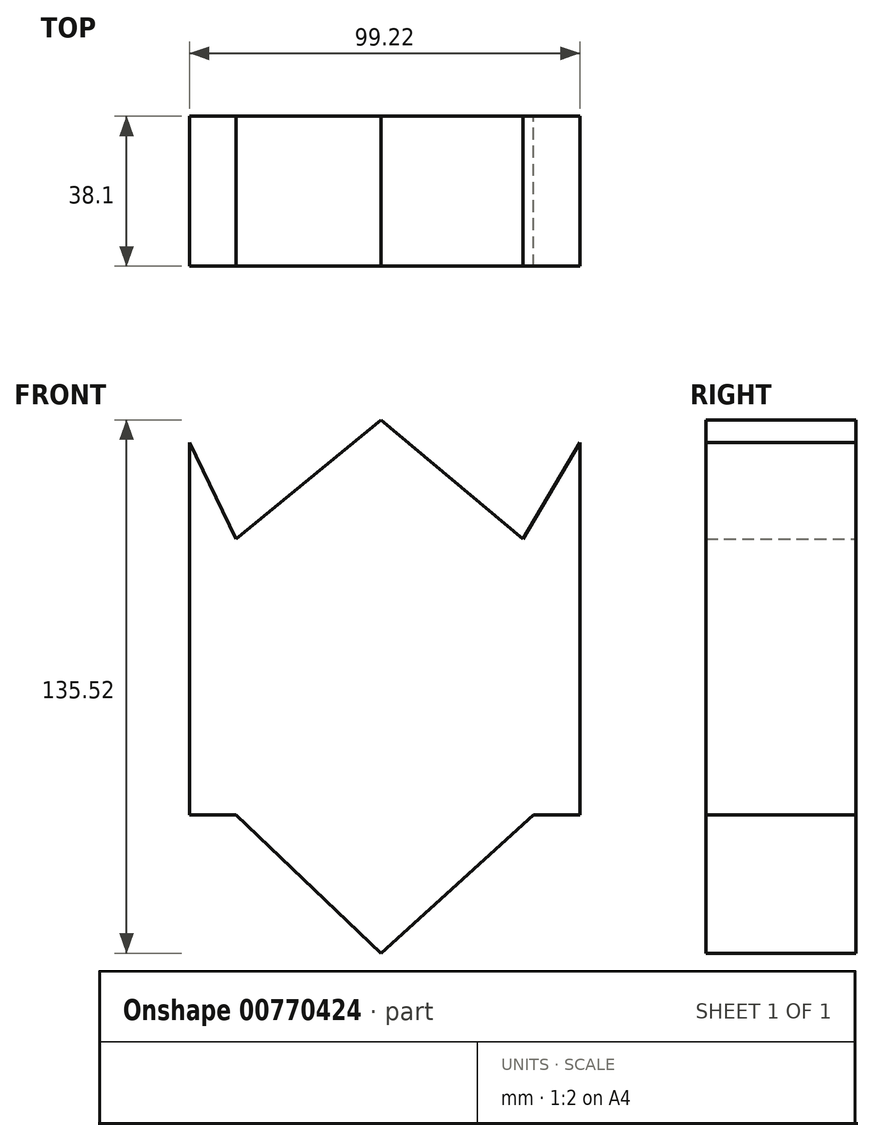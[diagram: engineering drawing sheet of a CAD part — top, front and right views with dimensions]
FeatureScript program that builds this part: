
annotation { "Feature Type Name" : "Feature", "Feature Type Description" : "" }
export const myFeature = defineFeature(function(context is Context, id is Id, definition is map)
    precondition{}
    {
        {
            var Q0;
            Q0=qCreatedBy(makeId("Front.planeOp"),FACE);
            var sketch = newSketch(context, id + "F0", { "sketchPlane" : qUnion([Q0])});
            skLineSegment(sketch, "E0", {"start": v(0, 0) * mm, "end": v(0, -69.27) * mm});
            skLineSegment(sketch, "E1", {"start": v(0, -69.27) * mm, "end": v(-36.9, -34.18) * mm});
            skLineSegment(sketch, "E2", {"start": v(-36.9, -34.18) * mm, "end": v(-48.7, -34.18) * mm});
            skLineSegment(sketch, "E3", {"start": v(-48.7, -34.18) * mm, "end": v(-48.7, 60.5) * mm});
            skLineSegment(sketch, "E4", {"start": v(-48.7, 60.5) * mm, "end": v(-36.9, 36) * mm});
            skLineSegment(sketch, "E5", {"start": v(-36.9, 36) * mm, "end": v(0, 66.25) * mm});
            skLineSegment(sketch, "E6", {"start": v(0, 66.25) * mm, "end": v(36, 36) * mm});
            skLineSegment(sketch, "E7", {"start": v(36, 36) * mm, "end": v(50.52, 60.5) * mm});
            skLineSegment(sketch, "E8", {"start": v(50.52, 60.5) * mm, "end": v(50.52, -34.18) * mm});
            skLineSegment(sketch, "E9", {"start": v(50.52, -34.18) * mm, "end": v(38.72, -34.18) * mm});
            skLineSegment(sketch, "E10", {"start": v(38.72, -34.18) * mm, "end": v(0, -69.27) * mm});
            skSolve(sketch);
        }
        {
            var Q0;
            Q0 = qSketchRegion(id + "F0", true);
            extrude(context, id + "F1", {"entities" : qUnion([Q0]), "depth" : 38.1 * mm, "offsetDistance" : 25.4 * mm});
        }
    });
